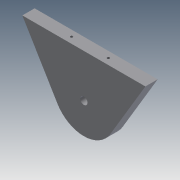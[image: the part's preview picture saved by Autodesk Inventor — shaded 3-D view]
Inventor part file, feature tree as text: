
AUTODESK INVENTOR PART (.ipt)
format: ipt  version: 2013 (Build 170138000, 138)  size: 84,992 bytes
history: native  units: mm
features: extrude x2, sketch x2
ambient origin geometry x8: Origin, YZ Plane, XZ Plane, XY Plane, X Axis, Y Axis, Z Axis, Center Point
bodies: Solid1 (feature_tree)
feature tree (4):
  extrude  "Extrusion1"  Depth=50.0mm
  extrude  "Extrusion2"  Depth=6.0mm
  sketch  "Sketch1"  dims[d4=50.0mm d5=50.0mm]
  sketch  "Sketch2"  dims[d6=100.0mm d7=6.0mm d8=10.0mm d9=0.0mm d11=2.0mm d12=2.0mm d13=10.0mm d14=0.0mm]
